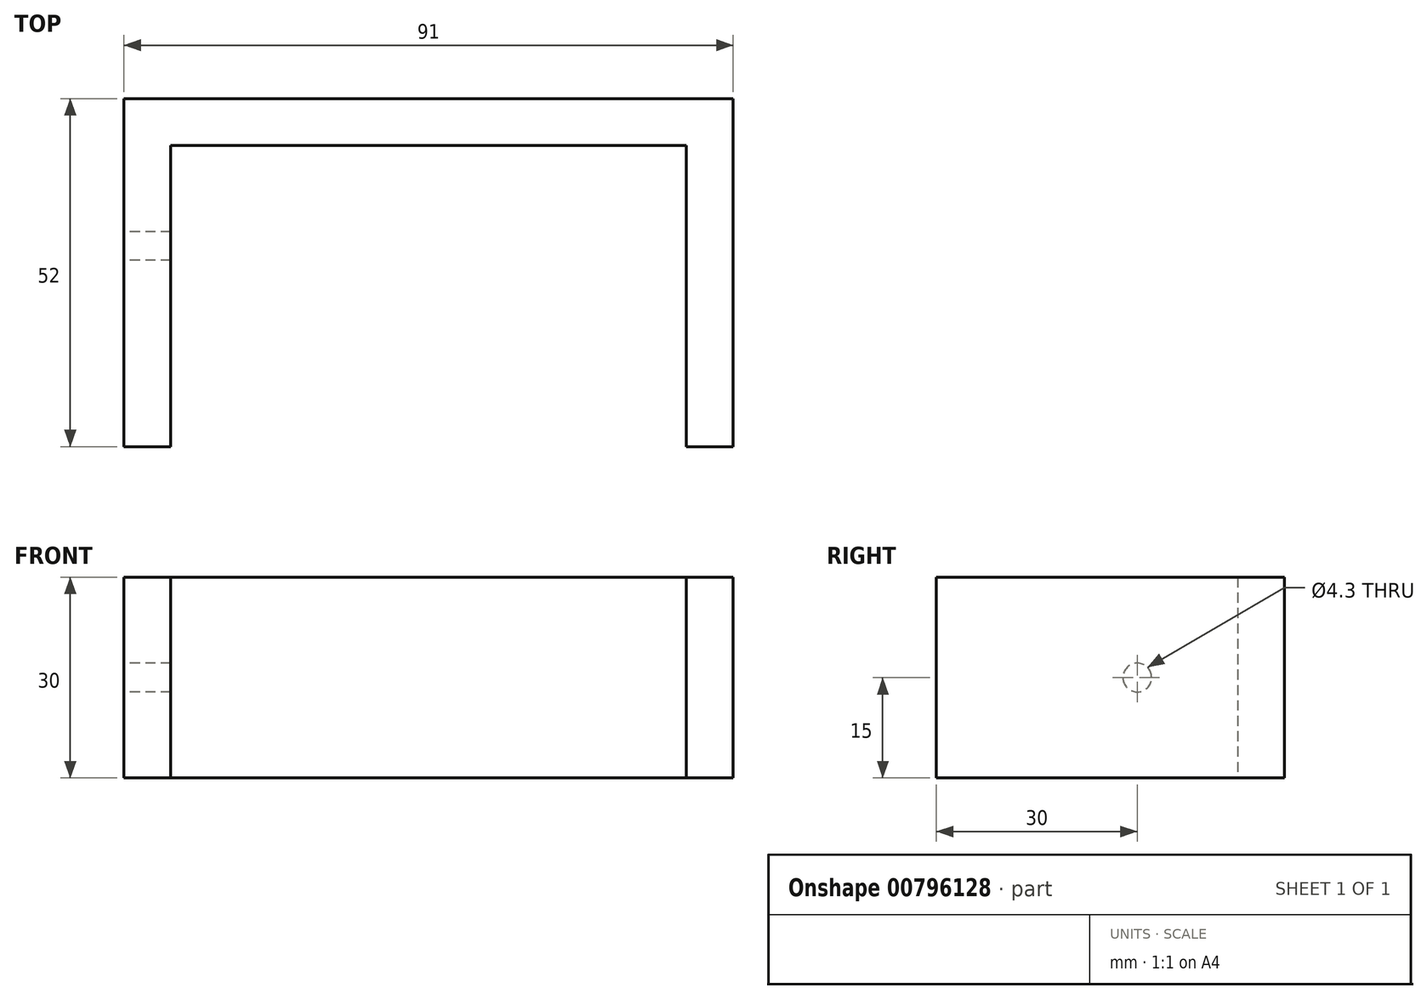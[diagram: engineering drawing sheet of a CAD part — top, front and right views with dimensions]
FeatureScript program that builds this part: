
annotation { "Feature Type Name" : "Feature", "Feature Type Description" : "" }
export const myFeature = defineFeature(function(context is Context, id is Id, definition is map)
    precondition{}
    {
        {
            var Q0;
            Q0=qCreatedBy(makeId("Top.planeOp"),FACE);
            var sketch = newSketch(context, id + "F0", { "sketchPlane" : qUnion([Q0])});
            skLineSegment(sketch, "E0.bottom", {"start": v(-45.5, 26) * mm, "end": v(45.5, 26) * mm});
            skLineSegment(sketch, "E0.left", {"start": v(-45.5, 26) * mm, "end": v(-45.5, -26) * mm});
            skLineSegment(sketch, "E0.right", {"start": v(45.5, 26) * mm, "end": v(45.5, -26) * mm});
            skPoint(sketch, "E0.middle", {"position": v(0, 0) * mm});
            skLineSegment(sketch, "E1", {"start": v(-38.5, -26) * mm, "end": v(-38.5, 19) * mm});
            skLineSegment(sketch, "E2", {"start": v(-38.5, 19) * mm, "end": v(38.5, 19) * mm});
            skLineSegment(sketch, "E3", {"start": v(38.5, 19) * mm, "end": v(38.5, -26) * mm});
            skLineSegment(sketch, "E4", {"start": v(-45.5, -26) * mm, "end": v(-38.5, -26) * mm});
            skLineSegment(sketch, "E5", {"start": v(38.5, -26) * mm, "end": v(45.5, -26) * mm});
            skSolve(sketch);
        }
        {
            var Q0;
            Q0=makeQuery(id+"F0.imprint","IMPRINT",FACE,{"disambiguationData":[TD([[makeQuery(id+"F0.imprint","IMPRINT",EDGE,{"derivedFrom":sQuery(id+"F0.wireOp",EDGE,"E0.bottom")}),-1.0]])]});
            extrude(context, id + "F1", {"entities" : qUnion([Q0]), "depth" : 30 * mm, "offsetDistance" : 25 * mm});
        }
        {
            var Q0;
            Q0=makeQuery(id+"F1.opExtrude","SWEPT_FACE",FACE,{"disambiguationData":[OSD([sQuery(id+"F0.wireOp",EDGE,"E0.left")])]});
            var sketch = newSketch(context, id + "F2", { "sketchPlane" : qUnion([Q0])});
            skPoint(sketch, "E6", {"position": v(-4, 15) * mm});
            skSolve(sketch);
        }
        {
            var Q0;
            Q0=sQuery(id+"F2.wireOp",VERTEX,"E6");
            var Q1;
            Q1=makeQuery(id+"F1.opExtrude","SWEPT_BODY",BODY,{"disambiguationData":[OSD([sQuery(id+"F0.wireOp",EDGE,"E0.bottom"),sQuery(id+"F0.wireOp",EDGE,"E0.left"),sQuery(id+"F0.wireOp",EDGE,"E0.right"),sQuery(id+"F0.wireOp",EDGE,"E1"),sQuery(id+"F0.wireOp",EDGE,"E2"),sQuery(id+"F0.wireOp",EDGE,"E3"),sQuery(id+"F0.wireOp",EDGE,"E4"),sQuery(id+"F0.wireOp",EDGE,"E5")])]});
            hole(context, id + "F3", {"style" : HoleStyle.SIMPLE, "endStyle" : HoleEndStyle.BLIND, "holeDiameter" : 4.3 * mm, "majorDiameter" : 5 * mm, "holeDepth" : 10 * mm, "isTappedThrough" : true, "tappedDepth" : 12 * mm, "tapClearance" : 3, "startFromSketch" : true, "locations" : qUnion([Q0]), "scope" : qUnion([Q1])});
        }
    });
